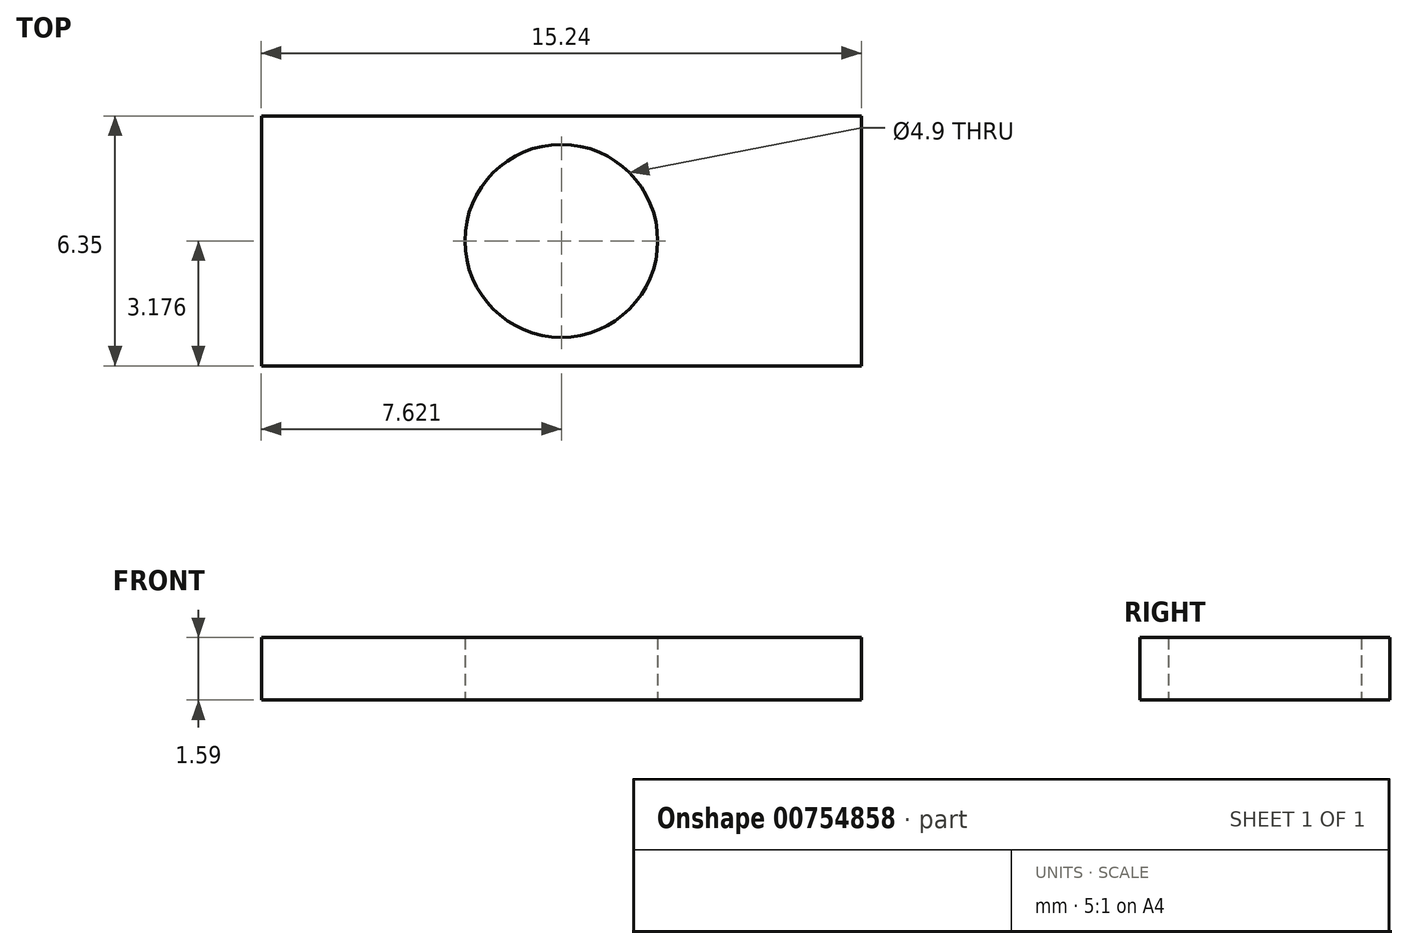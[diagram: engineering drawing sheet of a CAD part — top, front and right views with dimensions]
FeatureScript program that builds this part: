
annotation { "Feature Type Name" : "Feature", "Feature Type Description" : "" }
export const myFeature = defineFeature(function(context is Context, id is Id, definition is map)
    precondition{}
    {
        {
            var Q0;
            Q0=qCreatedBy(makeId("Top.planeOp"),FACE);
            var sketch = newSketch(context, id + "F0", { "sketchPlane" : qUnion([Q0])});
            skLineSegment(sketch, "E0.bottom", {"start": v(-54.23, 42.54) * mm, "end": v(-38.99, 42.54) * mm});
            skLineSegment(sketch, "E0.top", {"start": v(-54.23, 36.2) * mm, "end": v(-38.99, 36.2) * mm});
            skLineSegment(sketch, "E0.left", {"start": v(-54.23, 42.54) * mm, "end": v(-54.23, 36.2) * mm});
            skLineSegment(sketch, "E0.right", {"start": v(-38.99, 42.54) * mm, "end": v(-38.99, 36.2) * mm});
            skCircle(sketch, "E1", {"center": v(-46.6, 39.37) * mm, "radius": 2.45 * mm});
            skPoint(sketch, "E1.centerSnap0", {"position": v(-46.6, 36.2) * mm});
            skSolve(sketch);
        }
        {
            var Q0;
            Q0=makeQuery(id+"F0.imprint","IMPRINT",FACE,{"disambiguationData":[TD([[makeQuery(id+"F0.imprint","IMPRINT",EDGE,{"derivedFrom":sQuery(id+"F0.wireOp",EDGE,"E0.bottom")}),-1.0]])]});
            extrude(context, id + "F1", {"entities" : qUnion([Q0]), "depth" : 1.59 * mm, "offsetDistance" : 25.4 * mm});
        }
    });
